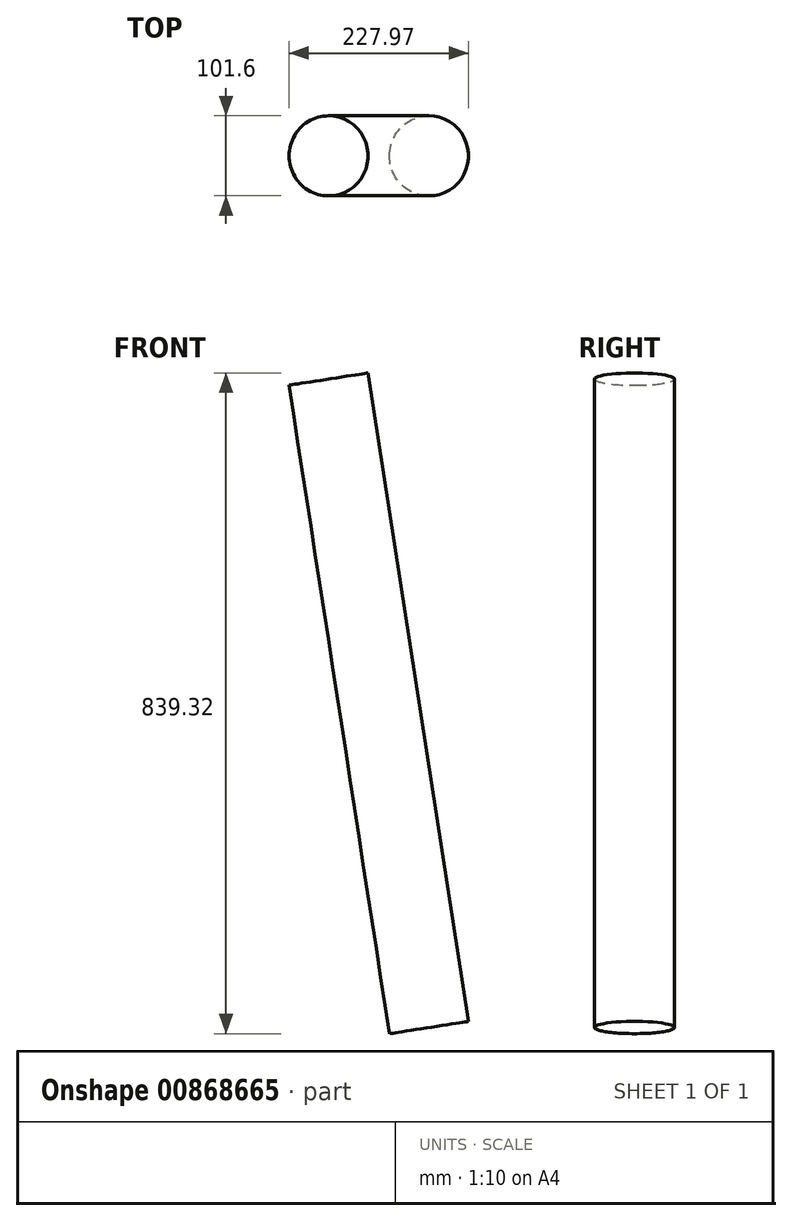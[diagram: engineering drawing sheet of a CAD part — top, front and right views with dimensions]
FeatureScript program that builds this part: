
annotation { "Feature Type Name" : "Feature", "Feature Type Description" : "" }
export const myFeature = defineFeature(function(context is Context, id is Id, definition is map)
    precondition{}
    {
        {
            var Q0;
            Q0=qCreatedBy(makeId("Front.planeOp"),FACE);
            var sketch = newSketch(context, id + "F0", { "sketchPlane" : qUnion([Q0])});
            skCircle(sketch, "E0", {"center": v(-30.23, -830.2) * mm, "radius": 107.95 * mm});
            skLineSegment(sketch, "E1", {"start": v(0, 0) * mm, "end": v(-97.65, -117.36) * mm});
            skLineSegment(sketch, "E2", {"start": v(-97.65, -117.36) * mm, "end": v(-28.34, -938.13) * mm});
            skLineSegment(sketch, "E3", {"start": v(0, 0) * mm, "end": v(87.01, 208.58) * mm});
            skLineSegment(sketch, "E4", {"start": v(97.7, 139.55) * mm, "end": v(225.27, -684.22) * mm});
            skLineSegment(sketch, "E5", {"start": v(97.7, 139.55) * mm, "end": v(87.01, 208.58) * mm});
            skCircle(sketch, "E6", {"center": v(0, 0) * mm, "radius": 31.75 * mm});
            skSolve(sketch);
        }
        {
            var Q0;
            Q0=sQuery(id+"F0.wireOp",EDGE,"E4");
            var Q1;
            Q1 = qBodyType(qCreatedBy(id + "F2" ,EDGE), BodyType.WIRE);
            cPlane(context, id + "F1", {"entities" : qUnion([Q0, Q1]), "cplaneType" : CPlaneType.MID_PLANE, "offset" : 25 * mm, "width" : 150 * mm, "height" : 150 * mm});
        }
        {
            var Q0;
            Q0=qCreatedBy(id+"F1.planeOp",FACE);
            var sketch = newSketch(context, id + "F2", { "sketchPlane" : qUnion([Q0])});
            skCircle(sketch, "E7", {"center": v(117.9, 0) * mm, "radius": 50.8 * mm});
            skSolve(sketch);
        }
        {
            var Q0;
            Q0=makeQuery(id+"F2.imprint","IMPRINT",FACE,{"disambiguationData":[TD([[makeQuery(id+"F2.imprint","IMPRINT",EDGE,{"derivedFrom":sQuery(id+"F2.wireOp",EDGE,"E7")}),1.0]])]});
            var Q1;
            Q1=sQuery(id+"F0.wireOp",EDGE,"E4");
            sweep(context, id + "F3", {"profiles" : qUnion([Q0]), "path" : qUnion([Q1])});
        }
    });
